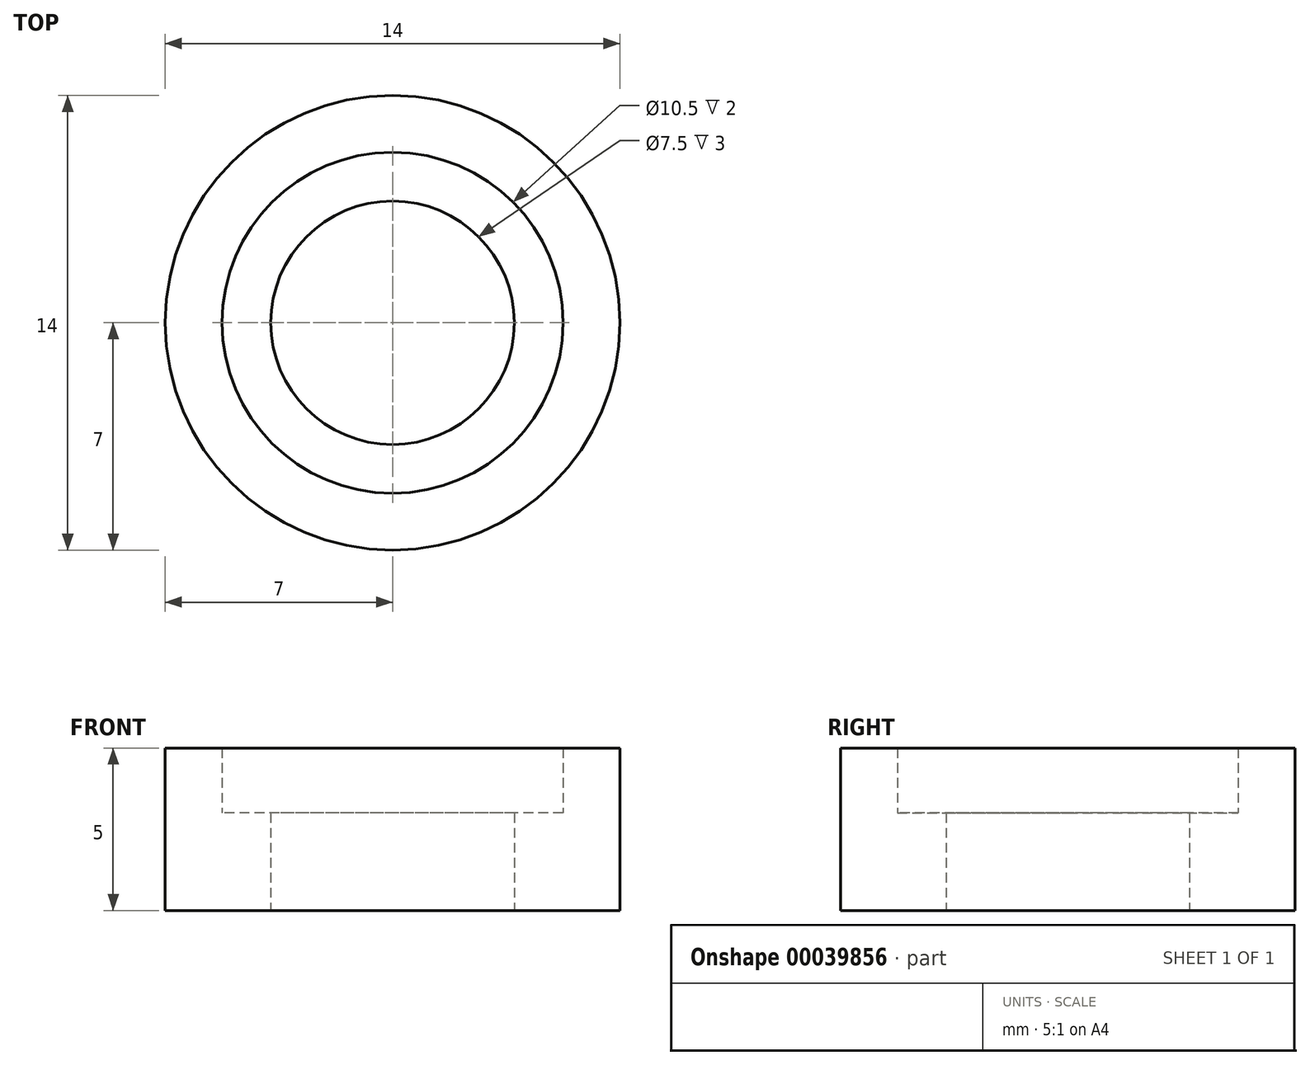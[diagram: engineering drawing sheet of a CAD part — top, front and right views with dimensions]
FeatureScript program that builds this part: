
annotation { "Feature Type Name" : "Feature", "Feature Type Description" : "" }
export const myFeature = defineFeature(function(context is Context, id is Id, definition is map)
    precondition{}
    {
        {
            var Q0;
            Q0=qCreatedBy(makeId("Top.planeOp"),FACE);
            var sketch = newSketch(context, id + "F0", { "sketchPlane" : qUnion([Q0])});
            skCircle(sketch, "E0", {"center": v(0, 0) * mm, "radius": 3.75 * mm});
            skCircle(sketch, "E1", {"center": v(0, 0) * mm, "radius": 5.25 * mm});
            skCircle(sketch, "E2", {"center": v(0, 0) * mm, "radius": 7 * mm});
            skLineSegment(sketch, "E3", {"start": v(3.75, 0) * mm, "end": v(-3.75, 0) * mm, "construction": true});
            skLineSegment(sketch, "E4", {"start": v(3.75, 0) * mm, "end": v(-1.75, 0) * mm});
            skLineSegment(sketch, "E5", {"start": v(-1.75, 4.95) * mm, "end": v(-1.75, -4.95) * mm});
            skSolve(sketch);
        }
        {
            var Q0;
            Q0=makeQuery(id+"F0.imprint","IMPRINT",FACE,{"disambiguationData":[TD([[makeQuery(id+"F0.imprint","IMPRINT",EDGE,{"derivedFrom":sQuery(id+"F0.wireOp",EDGE,"E2")}),1.0]])]});
            extrude(context, id + "F1", {"entities" : qUnion([Q0]), "depth" : 5 * mm});
        }
        {
            var Q0;
            {var subQ1=sQuery(id+"F0.wireOp",EDGE,"E0");var subQ6=makeQuery(id+"F0.imprint","INTERSECT",VERTEX,{"derivedFrom":[subQ1,sQuery(id+"F0.wireOp",EDGE,"E4")]});Q0=makeQuery(id+"F0.imprint","IMPRINT",FACE,{"disambiguationData":[TD([[makeQuery(id+"F0.imprint","IMPRINT",EDGE,{"disambiguationData":[TD([[subQ6,-1.0]])],"derivedFrom":subQ1}),-1.0]])]});}
            var Q1;
            {var subQ0=sQuery(id+"F0.wireOp",EDGE,"E5");var subQ1=sQuery(id+"F0.wireOp",EDGE,"E0");var subQ5=makeQuery(id+"F0.imprint","INTERSECT",VERTEX,{"disambiguationData":[OD(0.0)],"derivedFrom":[subQ1,subQ0]});Q1=makeQuery(id+"F0.imprint","IMPRINT",FACE,{"disambiguationData":[TD([[makeQuery(id+"F0.imprint","IMPRINT",EDGE,{"disambiguationData":[TD([[subQ5,-1.0]])],"derivedFrom":subQ1}),-1.0]])]});}
            extrude(context, id + "F2", {"entities" : qUnion([Q0, Q1]), "operationType" : NewBodyOperationType.ADD, "depth" : 3 * mm});
        }
    });
